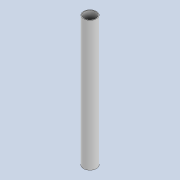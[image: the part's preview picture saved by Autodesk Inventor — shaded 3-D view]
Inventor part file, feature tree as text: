
AUTODESK INVENTOR PART (.ipt)
format: ipt  version: 2020 (Build 240168000, 168)  size: 73,728 bytes
history: native  units: mm
features: extrude x1, sketch x1
ambient origin geometry x8: Origin, YZ Plane, XZ Plane, XY Plane, X Axis, Y Axis, Z Axis, Center Point
bodies: Solid1 (feature_tree)
feature tree (2):
  extrude  "Extrusion1"  Depth=300.0mm
  sketch  "Sketch1"  dims[d0=30.0mm d1=27.0mm d2=300.0mm d3=0.0mm]
